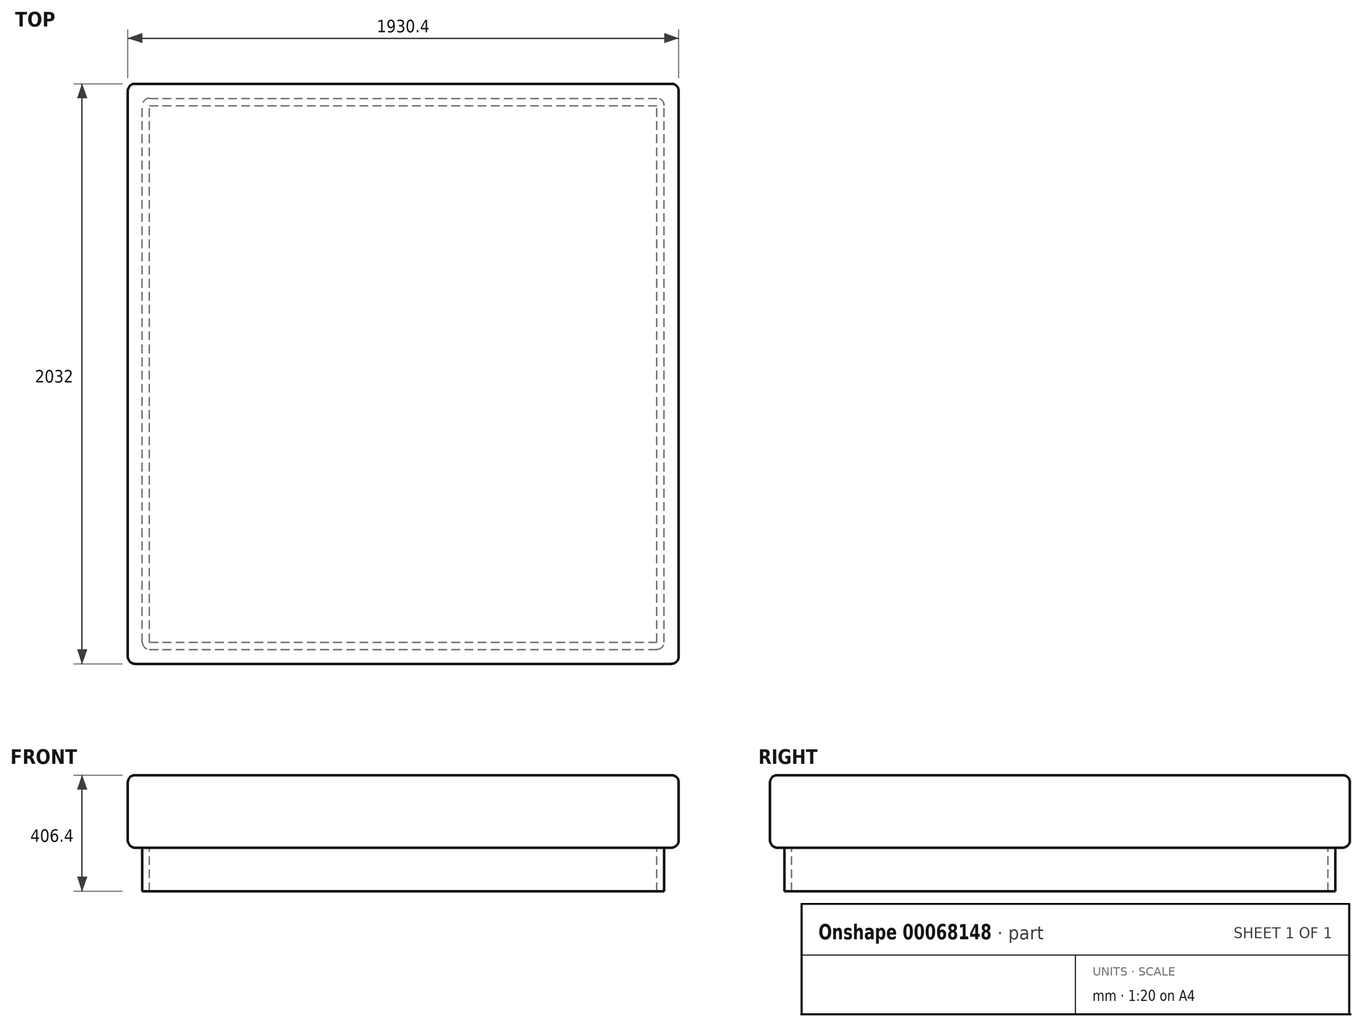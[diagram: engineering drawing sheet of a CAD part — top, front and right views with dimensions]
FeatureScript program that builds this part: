
annotation { "Feature Type Name" : "Feature", "Feature Type Description" : "" }
export const myFeature = defineFeature(function(context is Context, id is Id, definition is map)
    precondition{}
    {
        {
            var Q0;
            Q0=qCreatedBy(makeId("Top.planeOp"),FACE);
            var sketch = newSketch(context, id + "F0", { "sketchPlane" : qUnion([Q0])});
            skLineSegment(sketch, "E0.bottom", {"start": v(-999.58, -1030.05) * mm, "end": v(930.82, -1030.05) * mm});
            skLineSegment(sketch, "E0.top", {"start": v(-999.58, 1001.95) * mm, "end": v(930.82, 1001.95) * mm});
            skLineSegment(sketch, "E0.left", {"start": v(-999.58, -1030.05) * mm, "end": v(-999.58, 1001.95) * mm});
            skLineSegment(sketch, "E0.right", {"start": v(930.82, -1030.05) * mm, "end": v(930.82, 1001.95) * mm});
            skSolve(sketch);
        }
        {
            var Q0;
            Q0 = qSketchRegion(id + "F0", true);
            extrude(context, id + "F1", {"entities" : qUnion([Q0]), "oppositeDirection" : true, "depth" : 254 * mm});
        }
        {
            var Q0;
            Q0=makeQuery(id+"F1.opExtrude","CAP_FACE",FACE,{"disambiguationData":[OSD([sQuery(id+"F0.wireOp",EDGE,"E0.bottom"),sQuery(id+"F0.wireOp",EDGE,"E0.top"),sQuery(id+"F0.wireOp",EDGE,"E0.left"),sQuery(id+"F0.wireOp",EDGE,"E0.right")])],"isStart":false});
            var sketch = newSketch(context, id + "F2", { "sketchPlane" : qUnion([Q0])});
            skLineSegment(sketch, "E1.0", {"start": v(-948.78, 979.25) * mm, "end": v(880.02, 979.25) * mm});
            skLineSegment(sketch, "E1.1", {"start": v(-948.78, 979.25) * mm, "end": v(-948.78, -951.15) * mm});
            skLineSegment(sketch, "E1.2", {"start": v(-948.78, -951.15) * mm, "end": v(880.02, -951.15) * mm});
            skLineSegment(sketch, "E1.3", {"start": v(880.02, 979.25) * mm, "end": v(880.02, -951.15) * mm});
            skLineSegment(sketch, "E2.0", {"start": v(-923.38, 953.85) * mm, "end": v(854.62, 953.85) * mm});
            skLineSegment(sketch, "E2.1", {"start": v(-923.38, 953.85) * mm, "end": v(-923.38, -925.75) * mm});
            skLineSegment(sketch, "E2.2", {"start": v(-923.38, -925.75) * mm, "end": v(854.62, -925.75) * mm});
            skLineSegment(sketch, "E2.3", {"start": v(854.62, 953.85) * mm, "end": v(854.62, -925.75) * mm});
            skSolve(sketch);
        }
        {
            var Q0;
            Q0 = qSketchRegion(id + "F2", true);
            extrude(context, id + "F3", {"entities" : qUnion([Q0]), "operationType" : NewBodyOperationType.ADD, "depth" : 152.4 * mm});
        }
        {
            var Q0;
            Q0=makeQuery(id+"F1.opExtrude","SWEPT_FACE",FACE,{"disambiguationData":[OSD([sQuery(id+"F0.wireOp",EDGE,"E0.left")])]});
            var Q1;
            Q1=makeQuery(id+"F1.opExtrude","SWEPT_FACE",FACE,{"disambiguationData":[OSD([sQuery(id+"F0.wireOp",EDGE,"E0.top")])]});
            var Q2;
            Q2=makeQuery(id+"F1.opExtrude","SWEPT_FACE",FACE,{"disambiguationData":[OSD([sQuery(id+"F0.wireOp",EDGE,"E0.right")])]});
            var Q3;
            Q3=makeQuery(id+"F1.opExtrude","SWEPT_FACE",FACE,{"disambiguationData":[OSD([sQuery(id+"F0.wireOp",EDGE,"E0.bottom")])]});
            var Q4;
            Q4=makeQuery(id+"F1.opExtrude","CAP_FACE",FACE,{"disambiguationData":[OSD([sQuery(id+"F0.wireOp",EDGE,"E0.bottom"),sQuery(id+"F0.wireOp",EDGE,"E0.top"),sQuery(id+"F0.wireOp",EDGE,"E0.left"),sQuery(id+"F0.wireOp",EDGE,"E0.right")])],"isStart":true});
            var Q5;
            Q5=makeQuery(id+"F3.opExtrude","SWEPT_EDGE",EDGE,{"disambiguationData":[OSD([sQuery(id+"F2.wireOp",EDGE,"E1.0"),sQuery(id+"F2.wireOp",EDGE,"E1.3")])]});
            var Q6;
            Q6=makeQuery(id+"F3.opExtrude","SWEPT_EDGE",EDGE,{"disambiguationData":[OSD([sQuery(id+"F2.wireOp",EDGE,"E1.2"),sQuery(id+"F2.wireOp",EDGE,"E1.3")])]});
            var Q7;
            Q7=makeQuery(id+"F3.opExtrude","SWEPT_EDGE",EDGE,{"disambiguationData":[OSD([sQuery(id+"F2.wireOp",EDGE,"E1.1"),sQuery(id+"F2.wireOp",EDGE,"E1.2")])]});
            var Q8;
            Q8=makeQuery(id+"F3.opExtrude","SWEPT_EDGE",EDGE,{"disambiguationData":[OSD([sQuery(id+"F2.wireOp",EDGE,"E1.0"),sQuery(id+"F2.wireOp",EDGE,"E1.1")])]});
            fillet(context, id + "F4", {"entities" : qUnion([Q0, Q1, Q2, Q3, Q4, Q5, Q6, Q7, Q8]), "radius" : 25.4 * mm, "tangentPropagation" : true, "allowEdgeOverflow" : false});
        }
    });
